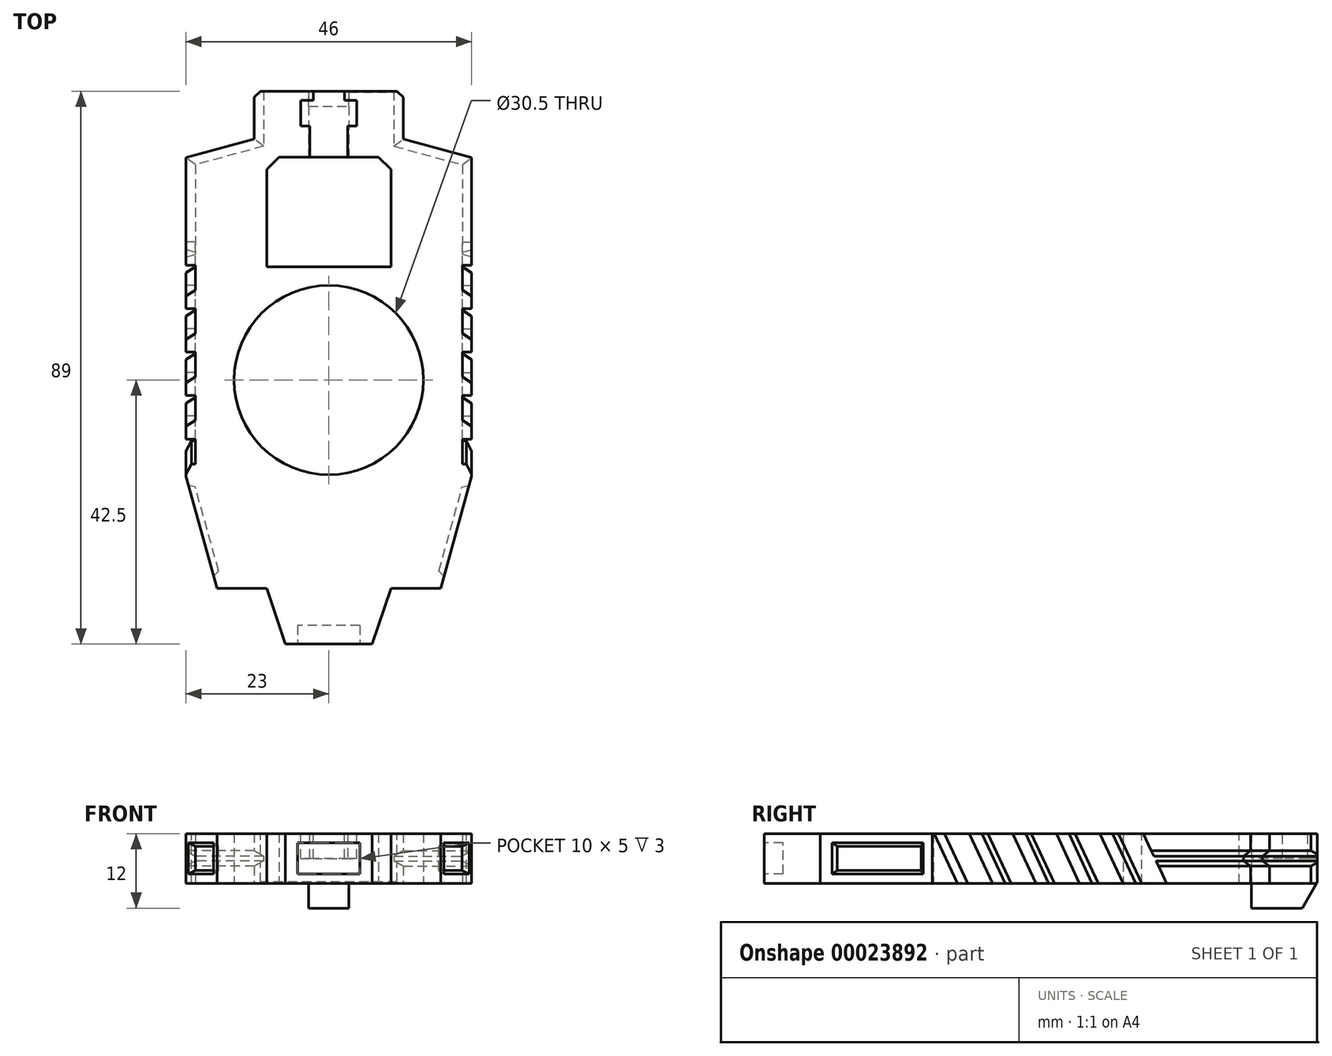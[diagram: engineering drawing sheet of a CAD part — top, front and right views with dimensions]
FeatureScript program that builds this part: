
annotation { "Feature Type Name" : "Feature", "Feature Type Description" : "" }
export const myFeature = defineFeature(function(context is Context, id is Id, definition is map)
    precondition{}
    {
        {
            var Q0;
            Q0=qCreatedBy(makeId("Top.planeOp"),FACE);
            var sketch = newSketch(context, id + "F0", { "sketchPlane" : qUnion([Q0])});
            skLineSegment(sketch, "E0", {"start": v(0, 46.5) * mm, "end": v(0, 15.25) * mm});
            skLineSegment(sketch, "E1", {"start": v(0, -42.5) * mm, "end": v(-7, -42.5) * mm});
            skLineSegment(sketch, "E2", {"start": v(-7, -42.5) * mm, "end": v(-10, -33.5) * mm});
            skLineSegment(sketch, "E3", {"start": v(-10, -33.5) * mm, "end": v(-18, -33.5) * mm});
            skLineSegment(sketch, "E4", {"start": v(-18, -33.5) * mm, "end": v(-23, -15.5) * mm});
            skLineSegment(sketch, "E5", {"start": v(-23, -15.5) * mm, "end": v(-23, 35.8) * mm});
            skLineSegment(sketch, "E6", {"start": v(-23, 35.8) * mm, "end": v(-12, 38.8) * mm});
            skLineSegment(sketch, "E7", {"start": v(-12, 38.8) * mm, "end": v(-12, 46.5) * mm});
            skLineSegment(sketch, "E8", {"start": v(-12, 46.5) * mm, "end": v(0, 46.5) * mm});
            skArc(sketch, "E9", {"start": v(0, 15.25) * mm, "mid": v(-15.25, 0) * mm, "end": v(0, -15.25) * mm});
            skLineSegment(sketch, "E10.trimOffspring", {"start": v(0, -15.25) * mm, "end": v(0, -42.5) * mm});
            skSolve(sketch);
        }
        {
            var Q0;
            Q0 = qSketchRegion(id + "F0", true);
            extrude(context, id + "F1", {"entities" : qUnion([Q0]), "endBound" : BoundingType.SYMMETRIC, "depth" : 8 * mm});
        }
        {
            var Q0;
            Q0=makeQuery(id+"F1.opExtrude","CAP_FACE",FACE,{"disambiguationData":[OSD([sQuery(id+"F0.wireOp",EDGE,"E0"),sQuery(id+"F0.wireOp",EDGE,"E1"),sQuery(id+"F0.wireOp",EDGE,"E2"),sQuery(id+"F0.wireOp",EDGE,"E3"),sQuery(id+"F0.wireOp",EDGE,"E4"),sQuery(id+"F0.wireOp",EDGE,"E5"),sQuery(id+"F0.wireOp",EDGE,"E6"),sQuery(id+"F0.wireOp",EDGE,"E7"),sQuery(id+"F0.wireOp",EDGE,"E8"),sQuery(id+"F0.wireOp",EDGE,"E9"),sQuery(id+"F0.wireOp",EDGE,"E10.trimOffspring")])],"isStart":false});
            var sketch = newSketch(context, id + "F2", { "sketchPlane" : qUnion([Q0])});
            skLineSegment(sketch, "E11", {"start": v(-26.5, -13.5) * mm, "end": v(-21.5, -13.5) * mm});
            skLineSegment(sketch, "E12", {"start": v(-21.5, -13.5) * mm, "end": v(-21.5, -9.5) * mm});
            skLineSegment(sketch, "E13", {"start": v(-21.5, -9.5) * mm, "end": v(-23, -9.5) * mm});
            skLineSegment(sketch, "E14", {"start": v(-23, -9.5) * mm, "end": v(-23, -6.5) * mm});
            skLineSegment(sketch, "E15", {"start": v(-23, -6.5) * mm, "end": v(-21.5, -6.5) * mm});
            skLineSegment(sketch, "E16.1.0.0", {"start": v(-21.5, -6.5) * mm, "end": v(-21.5, -2.5) * mm});
            skLineSegment(sketch, "E16.1.0.1", {"start": v(-21.5, -2.5) * mm, "end": v(-23, -2.5) * mm});
            skLineSegment(sketch, "E16.1.0.2", {"start": v(-23, -2.5) * mm, "end": v(-23, 0.5) * mm});
            skLineSegment(sketch, "E16.1.0.3", {"start": v(-23, 0.5) * mm, "end": v(-21.5, 0.5) * mm});
            skLineSegment(sketch, "E16.2.0.0", {"start": v(-21.5, 0.5) * mm, "end": v(-21.5, 4.5) * mm});
            skLineSegment(sketch, "E16.2.0.1", {"start": v(-21.5, 4.5) * mm, "end": v(-23, 4.5) * mm});
            skLineSegment(sketch, "E16.2.0.2", {"start": v(-23, 4.5) * mm, "end": v(-23, 7.5) * mm});
            skLineSegment(sketch, "E16.2.0.3", {"start": v(-23, 7.5) * mm, "end": v(-21.5, 7.5) * mm});
            skLineSegment(sketch, "E16.direction1", {"start": v(-21.5, -13.5) * mm, "end": v(-21.5, -6.5) * mm, "construction": true});
            skLineSegment(sketch, "E17.0.3.0", {"start": v(-21.5, 7.5) * mm, "end": v(-21.5, 11.5) * mm});
            skLineSegment(sketch, "E17.3.3.0", {"start": v(-21.5, 11.5) * mm, "end": v(-23, 11.5) * mm});
            skLineSegment(sketch, "E17.6.3.0", {"start": v(-23, 11.5) * mm, "end": v(-23, 14.5) * mm});
            skLineSegment(sketch, "E17.9.3.0", {"start": v(-23, 14.5) * mm, "end": v(-21.5, 14.5) * mm});
            skLineSegment(sketch, "E17.0.4.0", {"start": v(-21.5, 14.5) * mm, "end": v(-21.5, 18.5) * mm});
            skLineSegment(sketch, "E18", {"start": v(-21.5, 18.5) * mm, "end": v(-26.5, 18.5) * mm});
            skLineSegment(sketch, "E19", {"start": v(-26.5, 18.5) * mm, "end": v(-26.5, -13.5) * mm});
            skSolve(sketch);
        }
        {
            var Q0;
            Q0=makeQuery(id+"F1.opExtrude","SWEPT_FACE",FACE,{"disambiguationData":[OSD([sQuery(id+"F0.wireOp",EDGE,"E5")])]});
            var sketch = newSketch(context, id + "F3", { "sketchPlane" : qUnion([Q0])});
            skLineSegment(sketch, "E20", {"start": v(0, 4) * mm, "end": v(-3.73, -4) * mm});
            skSolve(sketch);
        }
        {
            var Q0;
            Q0 = qSketchRegion(id + "F2", true);
            var Q1;
            Q1 = qConstructionFilter(qBodyType(qCreatedBy(id + "F3" ,EDGE), BodyType.WIRE), ConstructionObject.NO);
            sweep(context, id + "F4", {"operationType" : NewBodyOperationType.REMOVE, "profiles" : qUnion([Q0]), "path" : qUnion([Q1])});
        }
        {
            var Q0;
            Q0=makeQuery(id+"F1.opExtrude","SWEPT_FACE",FACE,{"disambiguationData":[OSD([sQuery(id+"F0.wireOp",EDGE,"E8")])]});
            var sketch = newSketch(context, id + "F5", { "sketchPlane" : qUnion([Q0])});
            skLineSegment(sketch, "E21", {"start": v(10.5, 0.38) * mm, "end": v(10.5, -0.38) * mm});
            skLineSegment(sketch, "E22", {"start": v(10.5, -0.38) * mm, "end": v(12, -1.25) * mm});
            skLineSegment(sketch, "E23", {"start": v(12, -1.25) * mm, "end": v(12, 1.25) * mm});
            skLineSegment(sketch, "E24", {"start": v(12, 1.25) * mm, "end": v(10.5, 0.38) * mm});
            skPoint(sketch, "E25", {"position": v(10.5, 0) * mm});
            skSolve(sketch);
        }
        {
            var Q0;
            Q0 = qSketchRegion(id + "F5", true);
            var Q1;
            {var subQ0=sQuery(id+"F0.wireOp",EDGE,"E7");var subQ1=sQuery(id+"F0.wireOp",EDGE,"E8");Q1=makeQuery(id+"FjQXN8cGNRlZhI9_1.boolean.opBoolean","MERGE",EDGE,{"derivedFrom":[makeQuery(id+"F1.opExtrude","CAP_EDGE",EDGE,{"disambiguationData":[OSD([subQ0])],"isStart":false}),makeQuery(id+"FjQXN8cGNRlZhI9_1.opExtrude","SWEPT_EDGE",EDGE,{"disambiguationData":[OSD([subQ0,subQ1]),TDD([makeQuery(id+"F1.opExtrude","CAP_VERTEX",VERTEX,{"disambiguationData":[OSD([subQ0,subQ1])],"isStart":false})])]})]});}
            var Q2;
            Q2=makeQuery(id+"F1.opExtrude","CAP_EDGE",EDGE,{"disambiguationData":[OSD([sQuery(id+"F0.wireOp",EDGE,"E6")])],"isStart":false});
            var Q3;
            {var subQ0=sQuery(id+"F0.wireOp",EDGE,"E5");var subQ1=sQuery(id+"F0.wireOp",EDGE,"E6");Q3=makeQuery(id+"F4.boolean.opBoolean","SPLIT",EDGE,{"disambiguationData":[TD([makeQuery(id+"F1.opExtrude","SWEPT_FACE",FACE,{"disambiguationData":[OSD([subQ1])]})])],"derivedFrom":makeQuery(id+"F1.opExtrude","CAP_EDGE",EDGE,{"disambiguationData":[OSD([subQ0])],"isStart":false})});}
            sweep(context, id + "F6", {"operationType" : NewBodyOperationType.REMOVE, "profiles" : qUnion([Q0]), "path" : qUnion([Q1, Q2, Q3])});
        }
        {
            var Q0;
            Q0=makeQuery(id+"F1.opExtrude","SWEPT_FACE",FACE,{"disambiguationData":[OSD([sQuery(id+"F0.wireOp",EDGE,"E4")])]});
            var sketch = newSketch(context, id + "F7", { "sketchPlane" : qUnion([Q0])});
            skLineSegment(sketch, "E26.rect.bottom", {"start": v(25.46, 2.5) * mm, "end": v(10.28, 2.5) * mm});
            skLineSegment(sketch, "E26.rect.top", {"start": v(25.46, -2.5) * mm, "end": v(10.28, -2.5) * mm});
            skLineSegment(sketch, "E26.rect.left", {"start": v(25.46, 2.5) * mm, "end": v(25.46, -2.5) * mm});
            skLineSegment(sketch, "E26.rect.right", {"start": v(10.28, 2.5) * mm, "end": v(10.28, -2.5) * mm});
            skPoint(sketch, "E26.rect.middle", {"position": v(17.87, 0) * mm});
            skSolve(sketch);
        }
        {
            var Q0;
            Q0 = qSketchRegion(id + "F7", true);
            extrude(context, id + "F8", {"entities" : qUnion([Q0]), "operationType" : NewBodyOperationType.REMOVE, "oppositeDirection" : true, "depth" : 1 * mm, "hasDraft" : true, "draftAngle" : 30 * degree, "draftPullDirection" : true});
        }
        {
            var Q0;
            Q0=makeQuery(id+"F1.opExtrude","CAP_FACE",FACE,{"disambiguationData":[OSD([sQuery(id+"F0.wireOp",EDGE,"E0"),sQuery(id+"F0.wireOp",EDGE,"E1"),sQuery(id+"F0.wireOp",EDGE,"E2"),sQuery(id+"F0.wireOp",EDGE,"E3"),sQuery(id+"F0.wireOp",EDGE,"E4"),sQuery(id+"F0.wireOp",EDGE,"E5"),sQuery(id+"F0.wireOp",EDGE,"E6"),sQuery(id+"F0.wireOp",EDGE,"E7"),sQuery(id+"F0.wireOp",EDGE,"E8"),sQuery(id+"F0.wireOp",EDGE,"E9"),sQuery(id+"F0.wireOp",EDGE,"E10.trimOffspring")])],"isStart":true});
            var sketch = newSketch(context, id + "F9", { "sketchPlane" : qUnion([Q0])});
            skLineSegment(sketch, "E27.bottom", {"start": v(0, -46.5) * mm, "end": v(-3.25, -46.5) * mm});
            skLineSegment(sketch, "E27.top", {"start": v(0, -31.5) * mm, "end": v(-3.25, -31.5) * mm});
            skLineSegment(sketch, "E27.left", {"start": v(0, -46.5) * mm, "end": v(0, -31.5) * mm});
            skLineSegment(sketch, "E27.right", {"start": v(-3.25, -46.5) * mm, "end": v(-3.25, -31.5) * mm});
            skSolve(sketch);
        }
        {
            var Q0;
            Q0 = qSketchRegion(id + "F9", true);
            extrude(context, id + "F10", {"entities" : qUnion([Q0]), "operationType" : NewBodyOperationType.ADD, "depth" : 4 * mm});
        }
        {
            var Q0;
            Q0=makeQuery(id+"F1.opExtrude","CAP_FACE",FACE,{"disambiguationData":[OSD([sQuery(id+"F0.wireOp",EDGE,"E0"),sQuery(id+"F0.wireOp",EDGE,"E1"),sQuery(id+"F0.wireOp",EDGE,"E2"),sQuery(id+"F0.wireOp",EDGE,"E3"),sQuery(id+"F0.wireOp",EDGE,"E4"),sQuery(id+"F0.wireOp",EDGE,"E5"),sQuery(id+"F0.wireOp",EDGE,"E6"),sQuery(id+"F0.wireOp",EDGE,"E7"),sQuery(id+"F0.wireOp",EDGE,"E8"),sQuery(id+"F0.wireOp",EDGE,"E9"),sQuery(id+"F0.wireOp",EDGE,"E10.trimOffspring")])],"isStart":false});
            var sketch = newSketch(context, id + "F11", { "sketchPlane" : qUnion([Q0])});
            skLineSegment(sketch, "E28", {"start": v(0, 46.5) * mm, "end": v(-2.5, 46.5) * mm});
            skLineSegment(sketch, "E29", {"start": v(-2.5, 46.5) * mm, "end": v(-2.5, 45) * mm});
            skLineSegment(sketch, "E30", {"start": v(-2.5, 45) * mm, "end": v(-4.5, 45) * mm});
            skLineSegment(sketch, "E31", {"start": v(-4.5, 45) * mm, "end": v(-4.5, 40.9) * mm});
            skLineSegment(sketch, "E32", {"start": v(-4.5, 40.9) * mm, "end": v(-3.05, 40.9) * mm});
            skLineSegment(sketch, "E33", {"start": v(-3.05, 40.9) * mm, "end": v(-3.05, 20.25) * mm});
            skLineSegment(sketch, "E34", {"start": v(-3.05, 20.25) * mm, "end": v(0, 20.25) * mm});
            skLineSegment(sketch, "E35", {"start": v(0, 20.25) * mm, "end": v(0, 46.5) * mm});
            skSolve(sketch);
        }
        {
            var Q0;
            Q0 = qSketchRegion(id + "F11", true);
            extrude(context, id + "F12", {"entities" : qUnion([Q0]), "operationType" : NewBodyOperationType.REMOVE, "oppositeDirection" : true, "depth" : 4 * mm});
        }
        {
            var Q0;
            Q0=makeQuery(id+"F1.opExtrude","CAP_FACE",FACE,{"disambiguationData":[OSD([sQuery(id+"F0.wireOp",EDGE,"E0"),sQuery(id+"F0.wireOp",EDGE,"E1"),sQuery(id+"F0.wireOp",EDGE,"E2"),sQuery(id+"F0.wireOp",EDGE,"E3"),sQuery(id+"F0.wireOp",EDGE,"E4"),sQuery(id+"F0.wireOp",EDGE,"E5"),sQuery(id+"F0.wireOp",EDGE,"E6"),sQuery(id+"F0.wireOp",EDGE,"E7"),sQuery(id+"F0.wireOp",EDGE,"E8"),sQuery(id+"F0.wireOp",EDGE,"E9"),sQuery(id+"F0.wireOp",EDGE,"E10.trimOffspring")])],"isStart":false});
            var sketch = newSketch(context, id + "F13", { "sketchPlane" : qUnion([Q0])});
            skLineSegment(sketch, "E36.bottom", {"start": v(0, 35.9) * mm, "end": v(-10, 35.9) * mm});
            skLineSegment(sketch, "E36.top", {"start": v(0, 18.25) * mm, "end": v(-10, 18.25) * mm});
            skLineSegment(sketch, "E36.left", {"start": v(0, 35.9) * mm, "end": v(0, 18.25) * mm});
            skLineSegment(sketch, "E36.right", {"start": v(-10, 35.9) * mm, "end": v(-10, 18.25) * mm});
            skSolve(sketch);
        }
        {
            var Q0;
            Q0 = qSketchRegion(id + "F13", true);
            extrude(context, id + "F14", {"entities" : qUnion([Q0]), "operationType" : NewBodyOperationType.REMOVE, "endBound" : BoundingType.THROUGH_ALL, "oppositeDirection" : true, "depth" : 25 * mm});
        }
        {
            var Q0;
            Q0=makeQuery(id+"F14.boolean.opBoolean","COPY",EDGE,{"derivedFrom":makeQuery(id+"F14.opExtrude","SWEPT_EDGE",EDGE,{"disambiguationData":[OSD([sQuery(id+"F13.wireOp",EDGE,"E36.bottom"),sQuery(id+"F13.wireOp",EDGE,"E36.right")])]})});
            chamfer(context, id + "F15", {"entities" : qUnion([Q0]), "width" : 2 * mm, "tangentPropagation" : true});
        }
        {
            var Q0;
            {var subQ0=sQuery(id+"F0.wireOp",EDGE,"E7");var subQ1=sQuery(id+"F0.wireOp",EDGE,"E8");Q0=makeQuery(id+"F6.boolean.opBoolean","SPLIT",EDGE,{"disambiguationData":[TD([makeQuery(id+"F6.opSweep","SWEPT_FACE",FACE,{"disambiguationData":[OSD([subQ0,sQuery(id+"F5.wireOp",EDGE,"E22")])]})])],"derivedFrom":makeQuery(id+"F1.opExtrude","SWEPT_EDGE",EDGE,{"disambiguationData":[OSD([subQ0,subQ1])]})});}
            var Q1;
            {var subQ0=sQuery(id+"F0.wireOp",EDGE,"E7");var subQ1=sQuery(id+"F0.wireOp",EDGE,"E8");Q1=makeQuery(id+"F6.boolean.opBoolean","SPLIT",EDGE,{"disambiguationData":[TD([makeQuery(id+"F6.opSweep","SWEPT_FACE",FACE,{"disambiguationData":[OSD([subQ0,sQuery(id+"F5.wireOp",EDGE,"E24")])]})])],"derivedFrom":makeQuery(id+"F1.opExtrude","SWEPT_EDGE",EDGE,{"disambiguationData":[OSD([subQ0,subQ1])]})});}
            chamfer(context, id + "F16", {"entities" : qUnion([Q0, Q1]), "width" : 1 * mm, "tangentPropagation" : true});
        }
        {
            var Q0;
            Q0=makeQuery(id+"F4.boolean.opBoolean","COPY",EDGE,{"derivedFrom":makeQuery(id+"F4.opSweep","SWEPT_EDGE",EDGE,{"disambiguationData":[OSD([sQuery(id+"F0.wireOp",EDGE,"E5"),sQuery(id+"F2.wireOp",EDGE,"E17.6.3.0"),sQuery(id+"F2.wireOp",EDGE,"E17.9.3.0"),sQuery(id+"F3.wireOp",EDGE,"E20")])]})});
            var Q1;
            Q1=makeQuery(id+"F4.boolean.opBoolean","COPY",EDGE,{"derivedFrom":makeQuery(id+"F4.opSweep","SWEPT_EDGE",EDGE,{"disambiguationData":[OSD([sQuery(id+"F0.wireOp",EDGE,"E5"),sQuery(id+"F2.wireOp",EDGE,"E16.2.0.2"),sQuery(id+"F2.wireOp",EDGE,"E16.2.0.3"),sQuery(id+"F3.wireOp",EDGE,"E20")])]})});
            var Q2;
            Q2=makeQuery(id+"F4.boolean.opBoolean","COPY",EDGE,{"derivedFrom":makeQuery(id+"F4.opSweep","SWEPT_EDGE",EDGE,{"disambiguationData":[OSD([sQuery(id+"F0.wireOp",EDGE,"E5"),sQuery(id+"F2.wireOp",EDGE,"E16.1.0.2"),sQuery(id+"F2.wireOp",EDGE,"E16.1.0.3"),sQuery(id+"F3.wireOp",EDGE,"E20")])]})});
            var Q3;
            Q3=makeQuery(id+"F4.boolean.opBoolean","COPY",EDGE,{"derivedFrom":makeQuery(id+"F4.opSweep","SWEPT_EDGE",EDGE,{"disambiguationData":[OSD([sQuery(id+"F0.wireOp",EDGE,"E5"),sQuery(id+"F2.wireOp",EDGE,"E14"),sQuery(id+"F2.wireOp",EDGE,"E15"),sQuery(id+"F3.wireOp",EDGE,"E20")])]})});
            var Q4;
            Q4=makeQuery(id+"F4.boolean.opBoolean","INTERSECT",EDGE,{"derivedFrom":[makeQuery(id+"F1.opExtrude","SWEPT_FACE",FACE,{"disambiguationData":[OSD([sQuery(id+"F0.wireOp",EDGE,"E5")])]}),makeQuery(id+"F4.opSweep","SWEPT_FACE",FACE,{"disambiguationData":[OSD([sQuery(id+"F2.wireOp",EDGE,"E11"),sQuery(id+"F3.wireOp",EDGE,"E20")])]})]});
            chamfer(context, id + "F17", {"entities" : qUnion([Q0, Q1, Q2, Q3, Q4]), "chamferType" : ChamferType.OFFSET_ANGLE, "width" : 1.5 * mm, "oppositeDirection" : true, "angle" : 30 * degree, "tangentPropagation" : true});
        }
        {
            var Q0;
            Q0=makeQuery(id+"F10.opExtrude","CAP_EDGE",EDGE,{"disambiguationData":[OSD([sQuery(id+"F9.wireOp",EDGE,"E27.bottom")])],"isStart":false});
            chamfer(context, id + "F18", {"entities" : qUnion([Q0]), "chamferType" : ChamferType.OFFSET_ANGLE, "width" : 4.2 * mm, "oppositeDirection" : true, "angle" : 30 * degree, "tangentPropagation" : true});
        }
        {
            var Q0;
            Q0=makeQuery(id+"F1.opExtrude","SWEPT_BODY",BODY,{"disambiguationData":[OSD([sQuery(id+"F0.wireOp",EDGE,"E0"),sQuery(id+"F0.wireOp",EDGE,"E1"),sQuery(id+"F0.wireOp",EDGE,"E2"),sQuery(id+"F0.wireOp",EDGE,"E3"),sQuery(id+"F0.wireOp",EDGE,"E4"),sQuery(id+"F0.wireOp",EDGE,"E5"),sQuery(id+"F0.wireOp",EDGE,"E6"),sQuery(id+"F0.wireOp",EDGE,"E7"),sQuery(id+"F0.wireOp",EDGE,"E8"),sQuery(id+"F0.wireOp",EDGE,"E9"),sQuery(id+"F0.wireOp",EDGE,"E10.trimOffspring")])]});
            var Q1;
            Q1=makeQuery(id+"F1.opExtrude","SWEPT_FACE",FACE,{"disambiguationData":[OSD([sQuery(id+"F0.wireOp",EDGE,"E0")])]});
            mirror(context, id + "F19", {"operationType" : NewBodyOperationType.ADD, "entities" : qUnion([Q0]), "mirrorPlane" : qUnion([Q1])});
        }
        {
            var Q0;
            Q0=makeQuery(id+"F1.opExtrude","SWEPT_FACE",FACE,{"disambiguationData":[OSD([sQuery(id+"F0.wireOp",EDGE,"E1")])]});
            var sketch = newSketch(context, id + "F20", { "sketchPlane" : qUnion([Q0])});
            skLineSegment(sketch, "E37.rect.bottom", {"start": v(5, -2.5) * mm, "end": v(-5, -2.5) * mm});
            skLineSegment(sketch, "E37.rect.top", {"start": v(5, 2.5) * mm, "end": v(-5, 2.5) * mm});
            skLineSegment(sketch, "E37.rect.left", {"start": v(5, -2.5) * mm, "end": v(5, 2.5) * mm});
            skLineSegment(sketch, "E37.rect.right", {"start": v(-5, -2.5) * mm, "end": v(-5, 2.5) * mm});
            skPoint(sketch, "E37.rect.middle", {"position": v(0, 0) * mm});
            skSolve(sketch);
        }
        {
            var Q0;
            Q0 = qSketchRegion(id + "F20", true);
            extrude(context, id + "F21", {"entities" : qUnion([Q0]), "operationType" : NewBodyOperationType.REMOVE, "oppositeDirection" : true, "depth" : 3 * mm});
        }
    });
